# Revit family: Bath&ShowerMixer_(Built-in)_Vitra_MinimaxSSeries_A41994
name_source: partatom
category: Plumbing Fixtures
revit_build: Autodesk Revit 2017 (Build: 20160225_1515(x64)
units: mm (PartAtom-declared; Revit-internal decimal feet)

## family parameters
Cut with Voids When Loaded = No
Host = Face
OmniClass Number = 23.45.55.17
OmniClass Title = Mixing Faucets
Part Type = Normal
Room Calculation Point = No
Round Connector Dimension = Use Diameter
Shared = Yes

## types (8) — shared parameters
BIMobject category = Bath/Shower Mixer
CW Connection = Yes
Coating Material = Chrome
Color = Chrome
Connection Diameter (mm) = 15 mm  [stored 0.0492126 ft]
Default Elevation = 850 mm  [stored 2.78871 ft]
Description = Minimax S MC Bath / Shower filler mixer - C2 BlueStep cartridge
Design country = Turkey
HW Connection = Yes
Hot Water Supply (max.) = 80 °C
Hot Water temperature, factory set to = 38 °C
IFC Classification = Sanitary Terminal
Installation instructions = https://cdn.vitra.com.tr
Main Material = Brass
Manufacturer = Vitra
Manufacturer name = Vitra
Masterformat 2014 Code = 22 40 00
Masterformat 2014 Description = Plumbing Fixtures
Min. flow pressure of = 0.5 bar
Mounting type = Wall Mounted
NBS Referans Code = 45-35-70/315
NBS Referans Description = Water supply fittings for baths
Nominal Depth (mm) = 180 mm  [stored 0.590551 ft]
Nominal Height (mm) = 140 mm
Nominal Width (mm) = 225 mm  [stored 0.738189 ft]
Number Of Connections = 2
OmniClass Code = 23.45.55.17
OmniClass Description = Mixing Faucets
Product Guid = https://cdn.vitra.com.tr
Product Properties = Energy Saving
Product Type = Bath&Shower Mixer
Product certification = https://www.vitraglobal.com
Product family = Minimax S
Product group = Minimax S Bath&Shower Mixer
Range of Hot Water Supply = 5 - 65 °C
Range of flow pressure = 1 - 5 bar
Test Pressure = 16 bar
URL = https://vitraglobal.com
Uniclass 1.4 Code = L725111
Uniclass 1.4 Description = Mixer taps
Uniclass 2.0 Code = Pr_40_20_87_09
Uniclass 2.0 Description = Bath taps
Uniclass 2015 Code = Pr_40_20_87_09
Uniclass 2015 Name = Bath taps
Uniformat II Code = 22 40 00
Uniformat II Description = Plumbing Fixture
Vent Connection = No
Waste Connection = No
Weight Net (kg) = 1.83
Youtube = https://www.youtube.com

## per-type parameters (varying)
| type | Article No. (default) | Brand | Model | Product SKU | Product data url | Technical description | Warranty Period (Year) |
| Bath&ShowerMixer-Vitra-MinimaxS Series-A41994WSA | A41994WSA | Vitra | A41994WSA | A41994WSA | https://www.vitraglobal.com | https://www.vitraglobal.com | 7 Years |
| Bath&ShowerMixer-Vitra-MinimaxS Series-A41994TES | A41994TES | Vitra | A41994TES | A41994TES | https://www.vitraglobal.com | https://www.vitraglobal.com | 7 Years |
| Bath&ShowerMixer-Vitra-MinimaxS Series-A41994INV | A41994INV | Vitra | A41994INV | A41994INV | https://www.vitraglobal.com | https://www.vitraglobal.com | 7 Years |
| Bath&ShowerMixer-Vitra-MinimaxS Series-A41994EXP | A41994EXP | Vitra | A41994EXP | A41994EXP | https://www.vitraglobal.com | https://www.vitraglobal.com | 7 Years |
| Bath&ShowerMixer-Vitra-MinimaxS Series-A41994ENR | A41994ENR | Artema | A41994ENR | A41994ENR | https://www.vitraglobal.com | https://www.vitraglobal.com | 10 Years |
| Bath&ShowerMixer-Vitra-MinimaxS Series-A41994EKM | A41994EKM | Vitra | A41994EKM | A41994EKM | https://www.vitraglobal.com | https://www.vitraglobal.com | 7 Years |
| Bath&ShowerMixer-Vitra-MinimaxS Series-A41994EKF | A41994EKF | Vitra | A41994EKF | A41994EKF | https://www.vitra-bad.fr | https://cdn.vitra.com.tr | 7 Years |
| Bath&ShowerMixer-Vitra-MinimaxS Series-A41994 | A41994 | Artema | A41994 | A41994 | https://www.vitraglobal.com | https://www.vitraglobal.com | 10 Years |

note: [stored X ft] marks values corroborated as IEEE doubles in the binary element streams (Revit-internal decimal feet)

## geometry (parser evidence)
native form markers: Sweep x2
no freeform markers — native parametric forms only
